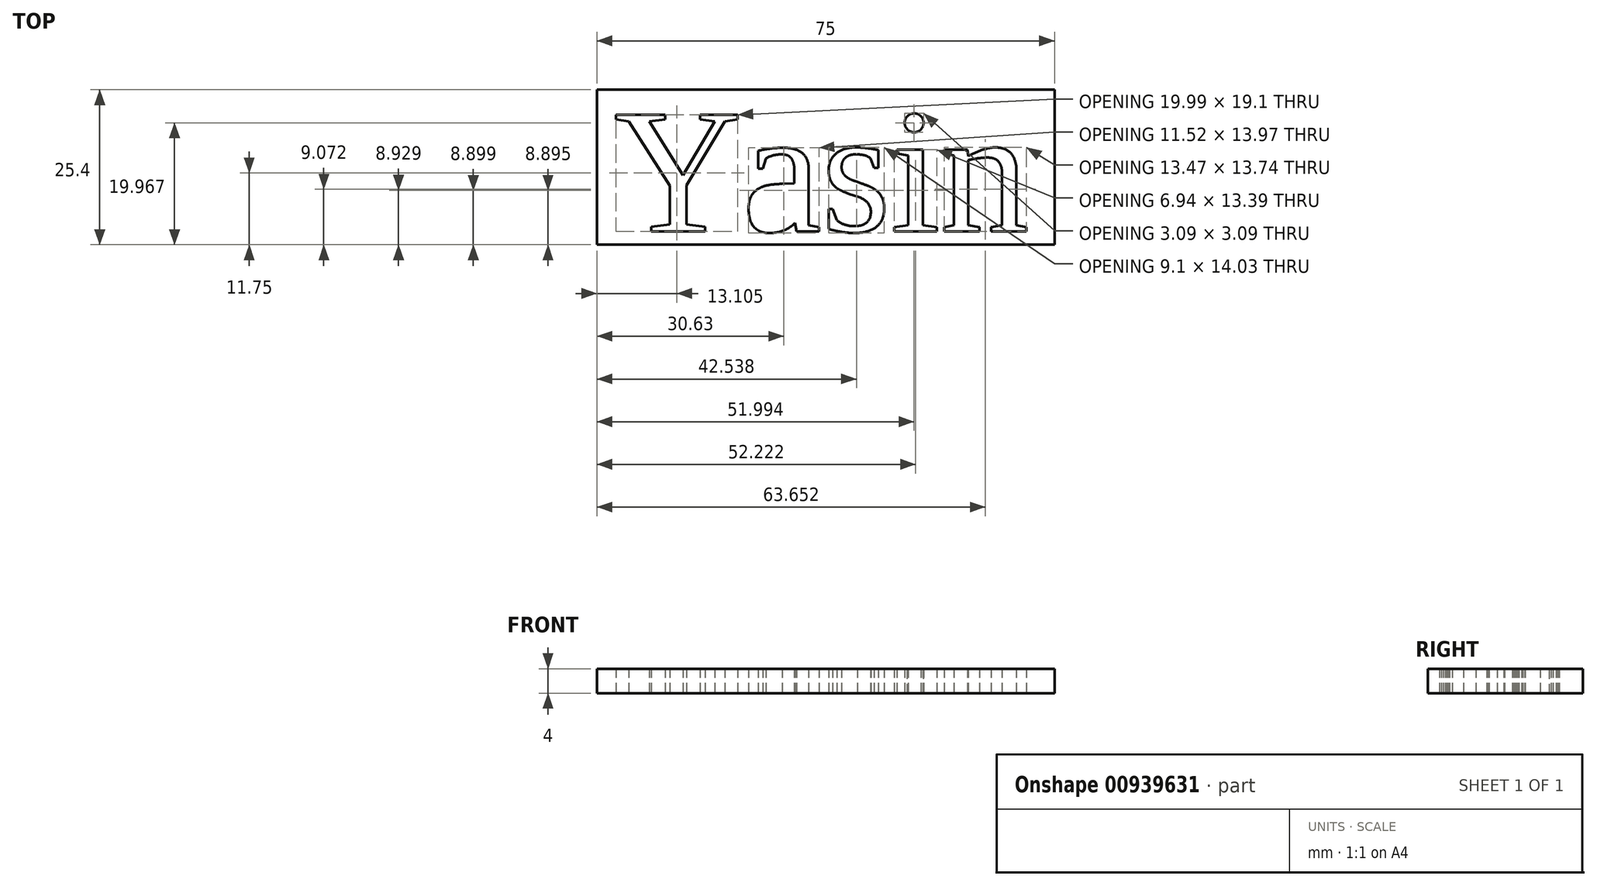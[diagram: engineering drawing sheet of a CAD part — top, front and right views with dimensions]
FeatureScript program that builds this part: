
annotation { "Feature Type Name" : "Feature", "Feature Type Description" : "" }
export const myFeature = defineFeature(function(context is Context, id is Id, definition is map)
    precondition{}
    {
        {
            var Q0;
            Q0=qCreatedBy(makeId("Top.planeOp"),FACE);
            var sketch = newSketch(context, id + "F0", { "sketchPlane" : qUnion([Q0])});
            skLineSegment(sketch, "E0.bottom", {"start": v(23.53, -7.45) * mm, "end": v(98.53, -7.45) * mm});
            skLineSegment(sketch, "E0.top", {"start": v(23.53, -32.85) * mm, "end": v(98.53, -32.85) * mm});
            skLineSegment(sketch, "E0.left", {"start": v(23.53, -7.45) * mm, "end": v(23.53, -32.85) * mm});
            skLineSegment(sketch, "E0.right", {"start": v(98.53, -7.45) * mm, "end": v(98.53, -32.85) * mm});
            skText(sketch, "E1", { "text": "Yasin", "fontName": "Tinos-Regular.ttf"});
            const initialGuessF0  = {"E1": [0.02631, -0.03065, 1, 0, 0.021]};
            skSetInitialGuess(sketch, initialGuessF0);
            skSolve(sketch);
        }
        {
            var Q0;
            Q0=makeQuery(id+"F0.imprint","IMPRINT",FACE,{"disambiguationData":[TD([[makeQuery(id+"F0.imprint","IMPRINT",EDGE,{"derivedFrom":sQuery(id+"F0.wireOp",EDGE,"E0.bottom")}),-1.0]])]});
            extrude(context, id + "F1", {"entities" : qUnion([Q0]), "depth" : 4 * mm, "offsetDistance" : 25 * mm});
        }
    });
